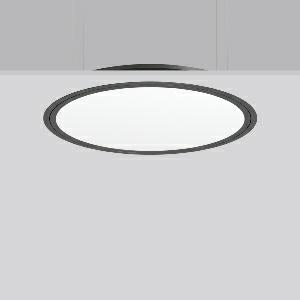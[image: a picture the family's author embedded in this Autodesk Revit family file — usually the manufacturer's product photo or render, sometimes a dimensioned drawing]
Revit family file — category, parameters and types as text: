
# Revit family: triona_round_e_312383_0031_1_12_7fe2
name_source: partatom
category: Lighting Fixtures
units: mm (PartAtom-declared; Revit-internal decimal feet)

## family parameters
Cut with Voids When Loaded = No
Host = Face
Light Source = No
Part Type = Normal
Room Calculation Point = No
Round Connector Dimension = Use Diameter
Shared = No

## types (1)
- TRIONA round E (1 x LED Modul 840, 6750 lm, 4000)
    Apparent Load = 70 VA
    CIE Flux Codes = 49 80 96 100 100
    Color Rendering = 80
    Color Temperature = 4000
    Default Elevation = 1800 mm
    Description = Series: TRIONA round
Decorative round LED recessed surface luminaire. Cover made of sheet steel, powder-coated. Frame made of aluminium, powder-coated. Recessed ring: aluminium extrusion profile, powder coated. Light emission through a diffuser: plastic, opal. Lightguide and diffuser made of non-yellowing plastic (PMMA). Lateral light emission (RZB SIDELITE technology) for above-average homogeneous light distribution. Suitable for installation in cavity ceilings. Tool-free mounting system thanks to the rocker arm mechanism (patent pending). Electronic ballast included. Very easy installation thanks to Plug+Play connection. 
Colour: anthracite metallic (DB703)
Diameter: 725 mm
Height: 2 mm
Cut-out diameter: 702 mm
Recess height: 100 mm
Luminaire: recess height: 89 mm
Lamp: LED
Socket: without socket
Colour temperature: 4000K
Colour rendering index (CRI): 80
System power: 70 W
Rated luminous flux: 6750 lm
Luminous efficiency: 96 lm/W
Control gear: Converter, dimmable, DALI
Protection class: I
Type of protection: IP 40
    Height = 0 mm  [stored 0 ft]
    Lamp = 1 x LED Modul 840
    Lamp Light Flux = 6750 lm
    Lamp count = 1
    Length = 725 mm
    Lifetime = 50000 h
    Luminous efficacy = 96 lm/W
    Manufacturer = RZB
    ModVariant = No
    Model = 312383.0031.1.12
    Mounting Place = Ceiling
    Mounting Type = Recessed
    Number of Poles = 1
    OnlyDefault = Yes
    Power Factor = 1
    Product Name = TRIONA round E
    Product group = Recessed modular luminaires
    ProductGroupID = 406
    Protection Class = Protection class I
    Protection Degree = IP 20
    RLX_Detail_Level = 1
    RLX_Emergency_Light_Flux = 0 lm
    RLX_Emergency_Type = 0
    RLX_Emergency_Type_DB = No
    RlxData = <blob elided: 38909 chars, md5=7c010c65>
    Socket = socket
    Standby Power = 0 W
    System Light Flux = 6750 lm
    System Power = 70 W
    Type Comments = Product without accessories
    Type Image = 312383.0031.12.jpg
    URL = http://relux.com
    VarID = ---
    Voltage = 230 V
    Voltage Range = 220-240 V
    Weight = 0.00 kg
    Width = 0 mm  [stored 0 ft]

note: [stored X ft] marks values corroborated as IEEE doubles in the binary element streams (Revit-internal decimal feet)

## geometry (parser evidence)
native form markers: Blend x4, Sweep x9
no freeform markers — native parametric forms only
